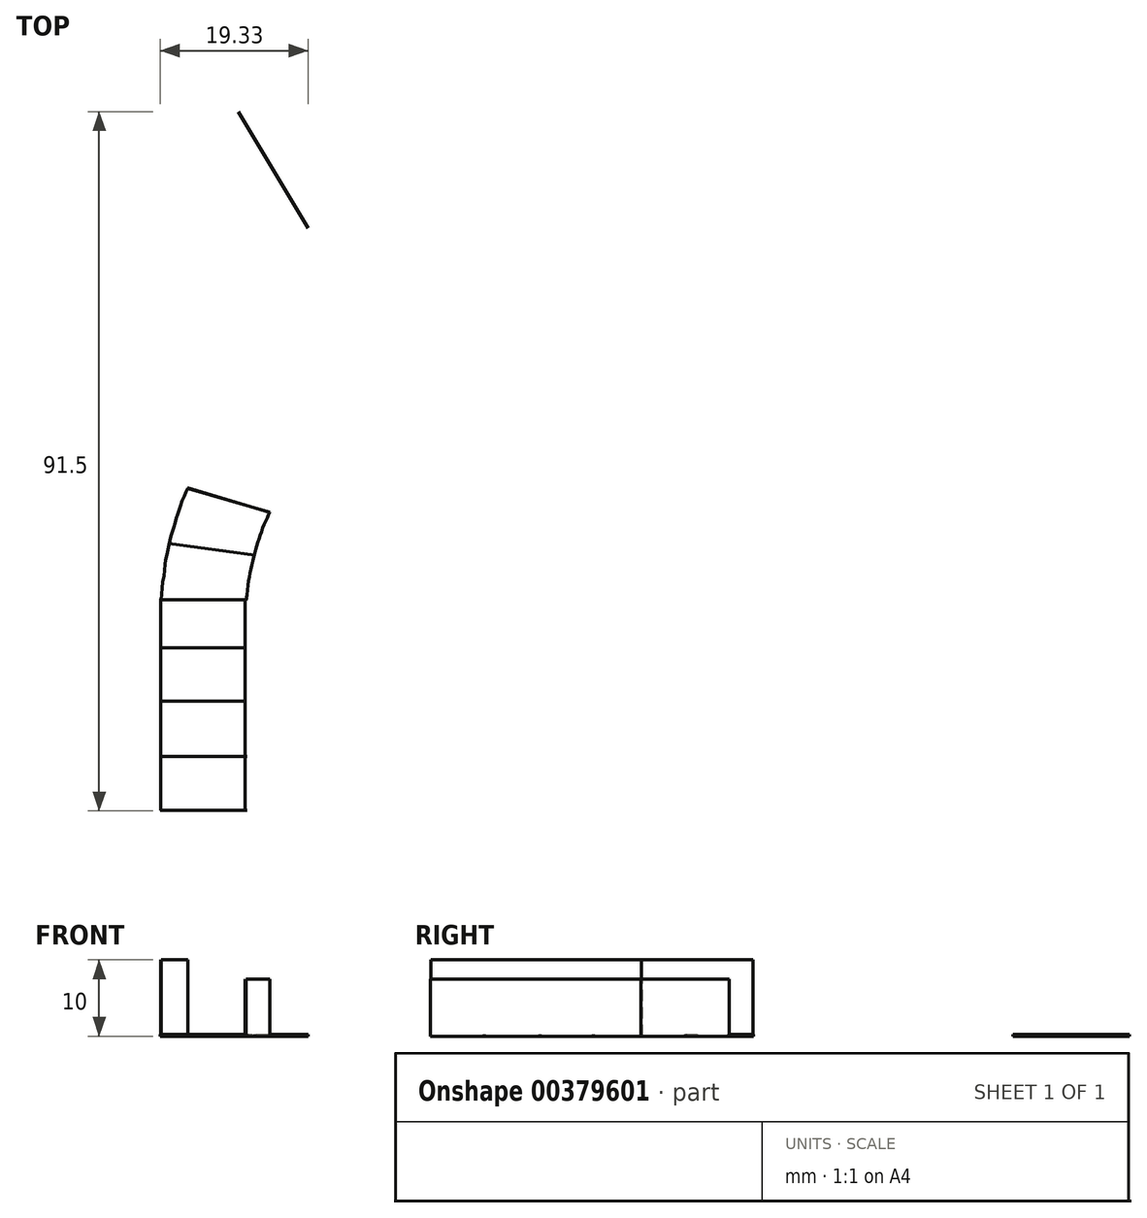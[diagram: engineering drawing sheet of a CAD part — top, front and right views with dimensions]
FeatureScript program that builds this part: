
annotation { "Feature Type Name" : "Feature", "Feature Type Description" : "" }
export const myFeature = defineFeature(function(context is Context, id is Id, definition is map)
    precondition{}
    {
        {
            var Q0;
            Q0=qCreatedBy(makeId("Top.planeOp"),FACE);
            var sketch = newSketch(context, id + "F0", { "sketchPlane" : qUnion([Q0])});
            skLineSegment(sketch, "E0.bottom", {"start": v(-44.6, -17.84) * mm, "end": v(-33.29, -17.84) * mm});
            skLineSegment(sketch, "E0.top", {"start": v(-44.6, -24.88) * mm, "end": v(-33.29, -24.88) * mm});
            skLineSegment(sketch, "E0.left", {"start": v(-44.6, -17.84) * mm, "end": v(-44.6, -24.88) * mm});
            skLineSegment(sketch, "E0.right", {"start": v(-33.29, -17.84) * mm, "end": v(-33.29, -24.88) * mm});
            skLineSegment(sketch, "E1.top", {"start": v(-44.6, -10.58) * mm, "end": v(-33.29, -10.58) * mm});
            skLineSegment(sketch, "E1.left", {"start": v(-44.6, -17.84) * mm, "end": v(-44.6, -10.58) * mm});
            skLineSegment(sketch, "E1.right", {"start": v(-33.29, -17.84) * mm, "end": v(-33.29, -10.58) * mm});
            skLineSegment(sketch, "E2.bottom", {"start": v(-44.6, -10.58) * mm, "end": v(-33.45, -10.58) * mm});
            skLineSegment(sketch, "E2.top", {"start": v(-44.6, -3.58) * mm, "end": v(-33.45, -3.58) * mm});
            skLineSegment(sketch, "E2.left", {"start": v(-44.6, -10.58) * mm, "end": v(-44.6, -3.58) * mm});
            skLineSegment(sketch, "E2.right", {"start": v(-33.45, -10.58) * mm, "end": v(-33.45, -3.58) * mm});
            skLineSegment(sketch, "E3.bottom", {"start": v(-33.45, -3.58) * mm, "end": v(-44.6, -3.58) * mm});
            skLineSegment(sketch, "E3.top", {"start": v(-33.45, 2.72) * mm, "end": v(-44.6, 2.72) * mm});
            skLineSegment(sketch, "E3.left", {"start": v(-33.45, -3.58) * mm, "end": v(-33.45, 2.72) * mm});
            skLineSegment(sketch, "E3.right", {"start": v(-44.6, -3.58) * mm, "end": v(-44.6, 2.72) * mm});
            skLineSegment(sketch, "E4", {"start": v(-32.21, 8.51) * mm, "end": v(-43.5, 10.05) * mm});
            skLineSegment(sketch, "E5", {"start": v(-30.28, 14.12) * mm, "end": v(-41.06, 17.36) * mm});
            skSolve(sketch);
        }
        {
            var Q0;
            Q0 = qSketchRegion(id + "F0", true);
            var Q1;
            Q1=sQuery(id+"F0.wireOp",EDGE,"E0.top");
            var Q2;
            Q2=sQuery(id+"F0.wireOp",EDGE,"E0.bottom");
            var Q3;
            Q3=sQuery(id+"F0.wireOp",EDGE,"E2.bottom");
            var Q4;
            Q4=sQuery(id+"F0.wireOp",EDGE,"E3.bottom");
            var Q5;
            Q5=sQuery(id+"F0.wireOp",EDGE,"E3.top");
            var Q6;
            Q6=sQuery(id+"F0.wireOp",EDGE,"E4");
            var Q7;
            Q7=sQuery(id+"F0.wireOp",EDGE,"E5");
            extrude(context, id + "F1", {"entities" : qUnion([Q0]), "bodyType" : ToolBodyType.SURFACE, "surfaceEntities" : qUnion([Q1, Q2, Q3, Q4, Q5, Q6, Q7]), "depth" : .2 * mm});
        }
        {
            var Q0;
            Q0=qCreatedBy(makeId("Top.planeOp"),FACE);
            var sketch = newSketch(context, id + "F2", { "sketchPlane" : qUnion([Q0])});
            skFitSpline(sketch, "E6", {"points": [v(-33.37, 2.66) * mm, v(-33.07, 4.9) * mm, v(-32.8, 6.4) * mm, v(-32.41, 8.1) * mm, v(-32.1, 9.45) * mm, v(-31.68, 10.7) * mm, v(-31.23, 12.04) * mm, v(-30.67, 13.3) * mm, v(-30.28, 14.21) * mm], "startDerivative": vector(1.94, 15.36) * mm, "endDerivative": vector(3.65, 8.56) * mm});
            skSolve(sketch);
        }
        {
            var Q0;
            Q0 = qSketchRegion(id + "F2", true);
            var Q1;
            Q1=sQuery(id+"F2.wireOp",EDGE,"E6");
            extrude(context, id + "F3", {"entities" : qUnion([Q0]), "bodyType" : ToolBodyType.SURFACE, "surfaceEntities" : qUnion([Q1]), "depth" : 7.5 * mm});
        }
        {
            var Q0;
            Q0=qCreatedBy(makeId("Top.planeOp"),FACE);
            var sketch = newSketch(context, id + "F4", { "sketchPlane" : qUnion([Q0])});
            skFitSpline(sketch, "E7", {"points": [v(-44.48, 2.72) * mm, v(-44.44, 3.7) * mm, v(-44.3, 4.95) * mm, v(-44.1, 6.13) * mm, v(-43.98, 7.15) * mm, v(-43.9, 7.91) * mm, v(-43.73, 8.72) * mm, v(-43.52, 9.57) * mm, v(-43.39, 10.2) * mm, v(-43.23, 10.87) * mm, v(-43.1, 11.47) * mm, v(-42.86, 12.18) * mm, v(-42.63, 12.94) * mm, v(-42.45, 13.55) * mm, v(-42.27, 14.03) * mm, v(-42.06, 14.67) * mm, v(-41.86, 15.37) * mm, v(-41.49, 16.27) * mm, v(-41.26, 16.73) * mm, v(-41.01, 17.31) * mm], "startDerivative": vector(0.38, 16.15) * mm, "endDerivative": vector(5.26, 13.08) * mm});
            skSolve(sketch);
        }
        {
            var Q0;
            Q0 = qSketchRegion(id + "F4", true);
            var Q1;
            Q1=sQuery(id+"F4.wireOp",EDGE,"E7");
            extrude(context, id + "F5", {"entities" : qUnion([Q0]), "bodyType" : ToolBodyType.SURFACE, "surfaceEntities" : qUnion([Q1]), "depth" : 10 * mm});
        }
        {
            var Q0;
            Q0=qCreatedBy(makeId("Top.planeOp"),FACE);
            var sketch = newSketch(context, id + "F6", { "sketchPlane" : qUnion([Q0])});
            skLineSegment(sketch, "E8", {"start": v(-33.5, 2.83) * mm, "end": v(-33.5, -24.93) * mm});
            skLineSegment(sketch, "E9", {"start": v(-44.46, 2.8) * mm, "end": v(-44.46, -24.97) * mm});
            skSolve(sketch);
        }
        {
            var Q0;
            Q0 = qSketchRegion(id + "F6", true);
            var Q1;
            Q1=sQuery(id+"F6.wireOp",EDGE,"E8");
            extrude(context, id + "F7", {"entities" : qUnion([Q0]), "bodyType" : ToolBodyType.SURFACE, "surfaceEntities" : qUnion([Q1]), "depth" : 7.5 * mm});
        }
        {
            var Q0;
            Q0=qCreatedBy(makeId("Top.planeOp"),FACE);
            var sketch = newSketch(context, id + "F8", { "sketchPlane" : qUnion([Q0])});
            skLineSegment(sketch, "E10", {"start": v(-44.55, -24.84) * mm, "end": v(-44.55, 2.8) * mm});
            skSolve(sketch);
        }
        {
            var Q0;
            Q0=sQuery(id+"F8.wireOp",EDGE,"E10");
            extrude(context, id + "F9", {"bodyType" : ToolBodyType.SURFACE, "surfaceEntities" : qUnion([Q0]), "depth" : 10 * mm});
        }
        {
            var Q0;
            Q0=qCreatedBy(makeId("Top.planeOp"),FACE);
            var sketch = newSketch(context, id + "F10", { "sketchPlane" : qUnion([Q0])});
            skLineSegment(sketch, "E11", {"start": v(-34.37, 66.57) * mm, "end": v(-25.27, 51.35) * mm});
            skSolve(sketch);
        }
        {
            var Q0;
            Q0 = qSketchRegion(id + "F10", true);
            var Q1;
            Q1=sQuery(id+"F10.wireOp",EDGE,"E11");
            extrude(context, id + "F11", {"entities" : qUnion([Q0]), "bodyType" : ToolBodyType.SURFACE, "surfaceEntities" : qUnion([Q1]), "depth" : 0.2 * mm});
        }
        {
            var Q0;
            Q0=qCreatedBy(makeId("Top.planeOp"),FACE);
            var sketch = newSketch(context, id + "F12", { "sketchPlane" : qUnion([Q0])});
            skLineSegment(sketch, "E12", {"start": v(-40.97, 17.24) * mm, "end": v(-30.37, 14.16) * mm});
            skSolve(sketch);
        }
        {
            var Q0;
            Q0=sQuery(id+"F12.wireOp",EDGE,"E12");
            extrude(context, id + "F13", {"bodyType" : ToolBodyType.SURFACE, "surfaceEntities" : qUnion([Q0]), "depth" : 0.2 * mm});
        }
    });
